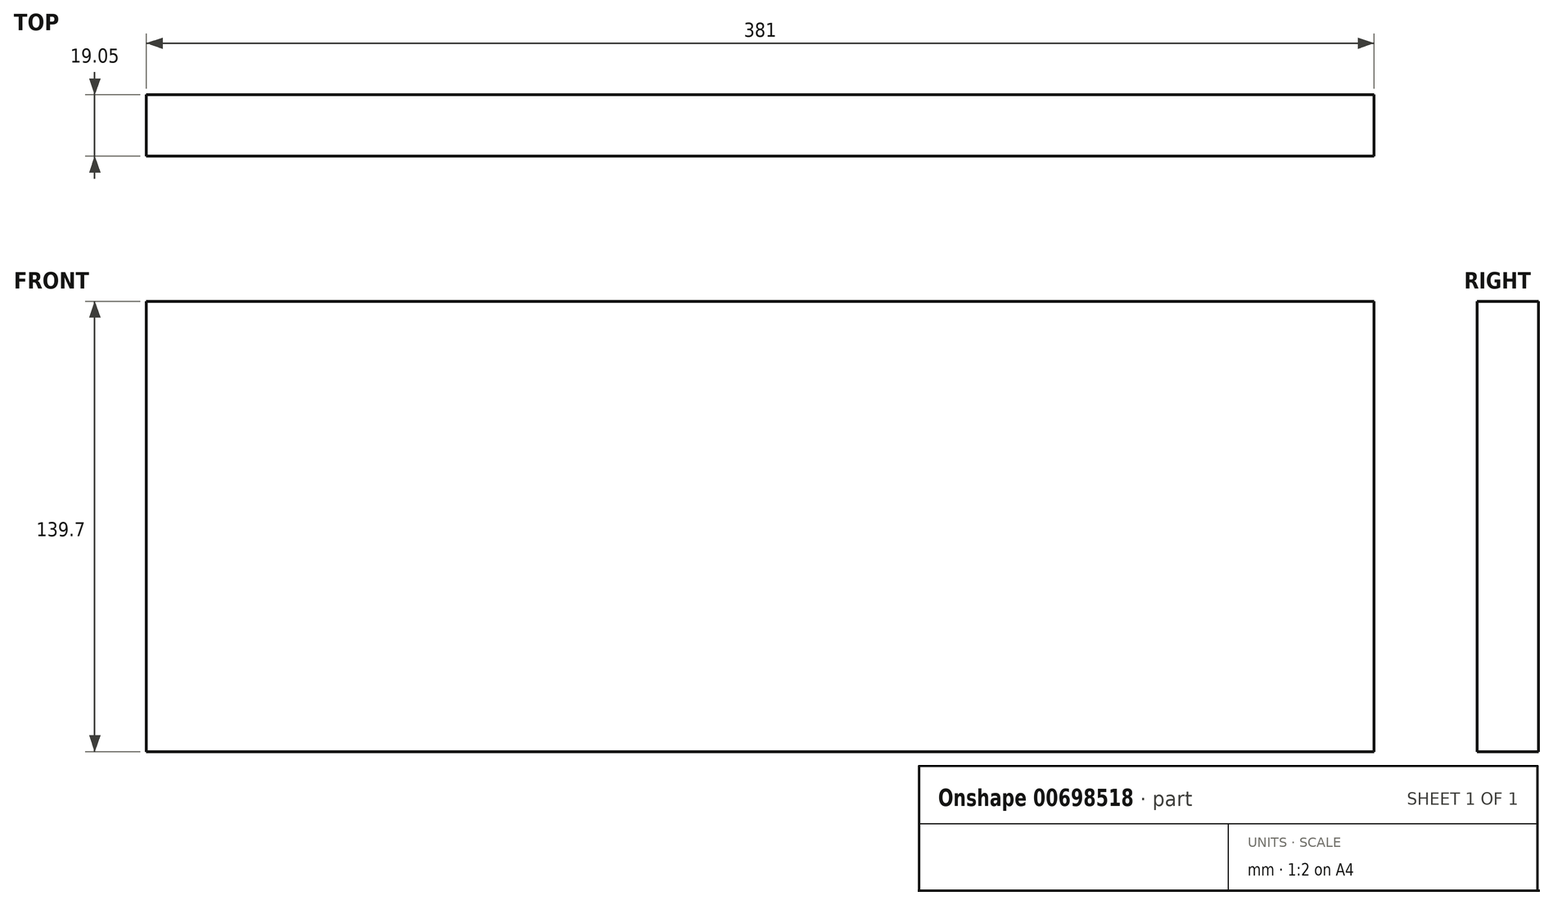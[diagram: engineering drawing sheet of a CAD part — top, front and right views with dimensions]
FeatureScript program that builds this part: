
annotation { "Feature Type Name" : "Feature", "Feature Type Description" : "" }
export const myFeature = defineFeature(function(context is Context, id is Id, definition is map)
    precondition{}
    {
        {
            var Q0;
            Q0=qCreatedBy(makeId("Front.planeOp"),FACE);
            var sketch = newSketch(context, id + "F0", { "sketchPlane" : qUnion([Q0])});
            skLineSegment(sketch, "E0.bottom", {"start": v(-195.83, -93.37) * mm, "end": v(185.17, -93.37) * mm});
            skLineSegment(sketch, "E0.top", {"start": v(-195.83, 46.33) * mm, "end": v(185.17, 46.33) * mm});
            skLineSegment(sketch, "E0.left", {"start": v(-195.83, -93.37) * mm, "end": v(-195.83, 46.33) * mm});
            skLineSegment(sketch, "E0.right", {"start": v(185.17, -93.37) * mm, "end": v(185.17, 46.33) * mm});
            skSolve(sketch);
        }
        {
            var Q0;
            Q0 = qSketchRegion(id + "F0", true);
            extrude(context, id + "F1", {"entities" : qUnion([Q0]), "depth" : 19.05 * mm, "offsetDistance" : 25.4 * mm});
        }
    });
